# Revit family: Sink-Pedestal-KOHLER-Folio-K-11340K_1
name_source: partatom
category: Specialty Equipment
units: mm (PartAtom-declared; Revit-internal decimal feet)

## family parameters
Cut with Voids When Loaded = No
Host = Face
OmniClass Number = 23.31.25.00
OmniClass Title = Toilet and Bath Specialties
Part Type = Normal
Room Calculation Point = No
Round Connector Dimension = Use Diameter
Shared = No

## types (1)
- 0-White
    ADA Compliant = No
    Assembly Code = C1030200
    Date Modified = 02/02/2023
    Default Elevation = 25"
    Description = Shroud
    Finish = Kohler-Vitreous_China-0-White
    Height = 10 3/16"
    Length = 11 7/16"
    Manufacturer = Kohler Co.
    Master Format 2014 = 10 28 16
    Master Format 2014 Name = Bath Accessories
    Material = Vitreous China
    Model = K-11340K-0
    Product Name = Folio
    Type = 1
    URL = https://www.kohlerasiapacific.com
    WaterSense Certified = No
    Width = 9 1/4"

## geometry (parser evidence)
native form markers: Sweep x5
no freeform markers — native parametric forms only
